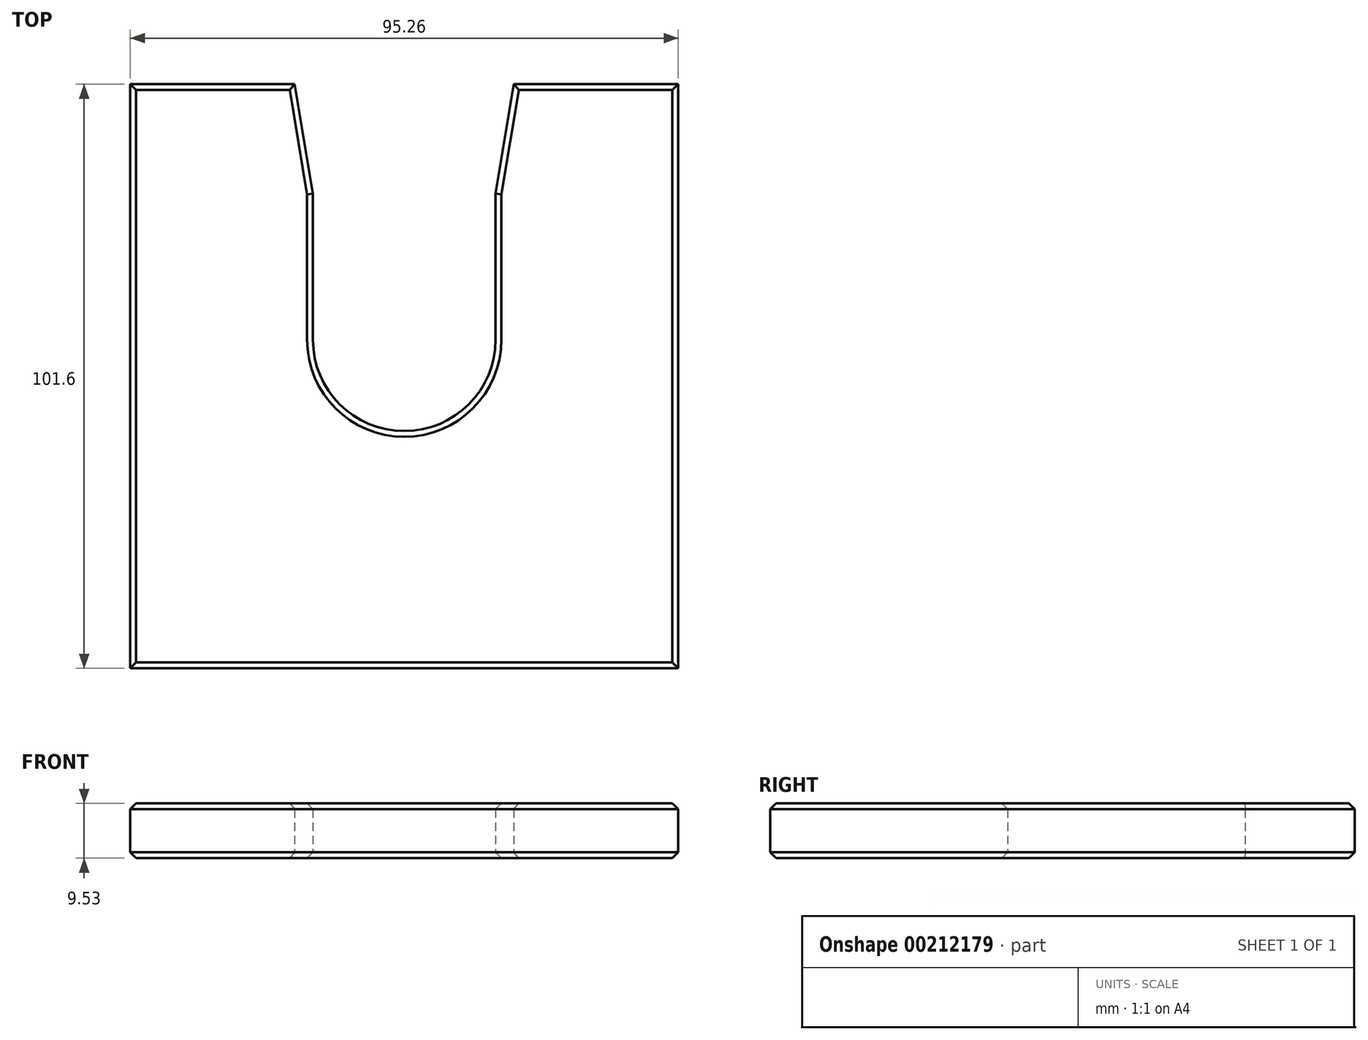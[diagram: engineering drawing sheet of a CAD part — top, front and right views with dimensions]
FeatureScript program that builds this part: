
annotation { "Feature Type Name" : "Feature", "Feature Type Description" : "" }
export const myFeature = defineFeature(function(context is Context, id is Id, definition is map)
    precondition{}
    {
        {
            var Q0;
            Q0=qCreatedBy(makeId("Top.planeOp"),FACE);
            var sketch = newSketch(context, id + "F0", { "sketchPlane" : qUnion([Q0])});
            skLineSegment(sketch, "E0.bottom", {"start": v(-47.62, 50.8) * mm, "end": v(-19.05, 50.8) * mm});
            skLineSegment(sketch, "E0.top", {"start": v(-47.63, -50.8) * mm, "end": v(47.62, -50.8) * mm});
            skLineSegment(sketch, "E0.left", {"start": v(-47.62, 50.8) * mm, "end": v(-47.63, -50.8) * mm});
            skLineSegment(sketch, "E0.right", {"start": v(47.63, 50.8) * mm, "end": v(47.62, -50.8) * mm});
            skPoint(sketch, "E0.middle", {"position": v(0, 0) * mm});
            skLineSegment(sketch, "E1", {"start": v(0, 50.8) * mm, "end": v(0, 6.35) * mm, "construction": true});
            skPoint(sketch, "E1.endSnap0", {"position": v(0, 50.8) * mm});
            skArc(sketch, "E2.0.endCap", {"start": v(15.88, 6.35) * mm, "mid": v(0, -9.53) * mm, "end": v(-15.87, 6.35) * mm});
            skLineSegment(sketch, "E2.0.left", {"start": v(15.88, 31.75) * mm, "end": v(15.88, 6.35) * mm});
            skLineSegment(sketch, "E2.0.right", {"start": v(-15.87, 31.75) * mm, "end": v(-15.87, 6.35) * mm});
            skLineSegment(sketch, "E3.0", {"start": v(-19.05, 50.8) * mm, "end": v(-19.05, 6.35) * mm, "construction": true});
            skLineSegment(sketch, "E4.0", {"start": v(19.05, 50.8) * mm, "end": v(19.05, 6.35) * mm, "construction": true});
            skLineSegment(sketch, "E5", {"start": v(19.05, 31.75) * mm, "end": v(-19.05, 31.75) * mm, "construction": true});
            skLineSegment(sketch, "E6", {"start": v(15.88, 31.75) * mm, "end": v(19.05, 50.8) * mm});
            skLineSegment(sketch, "E7", {"start": v(-15.87, 31.75) * mm, "end": v(-19.05, 50.8) * mm});
            skLineSegment(sketch, "E8.trimOffspring", {"start": v(19.05, 50.8) * mm, "end": v(47.63, 50.8) * mm});
            skLineSegment(sketch, "E9.trimOffspring", {"start": v(-15.87, 50.8) * mm, "end": v(0, 50.8) * mm});
            skSolve(sketch);
        }
        {
            var Q0;
            Q0=makeQuery(id+"F0.imprint","IMPRINT",FACE,{"disambiguationData":[TD([[makeQuery(id+"F0.imprint","IMPRINT",EDGE,{"derivedFrom":sQuery(id+"F0.wireOp",EDGE,"E0.bottom")}),-1.0]])]});
            extrude(context, id + "F1", {"entities" : qUnion([Q0]), "depth" : 9.52 * mm});
        }
        {
            var Q0;
            Q0=makeQuery(id+"F1.opExtrude","CAP_FACE",FACE,{"disambiguationData":[OSD([sQuery(id+"F0.wireOp",EDGE,"E0.bottom"),sQuery(id+"F0.wireOp",EDGE,"E0.top"),sQuery(id+"F0.wireOp",EDGE,"E0.left"),sQuery(id+"F0.wireOp",EDGE,"E0.right"),sQuery(id+"F0.wireOp",EDGE,"E2.0.endCap"),sQuery(id+"F0.wireOp",EDGE,"E2.0.left"),sQuery(id+"F0.wireOp",EDGE,"E2.0.right"),sQuery(id+"F0.wireOp",EDGE,"E6"),sQuery(id+"F0.wireOp",EDGE,"E7"),sQuery(id+"F0.wireOp",EDGE,"E8.trimOffspring")])],"isStart":false});
            var Q1;
            Q1=makeQuery(id+"F1.opExtrude","CAP_FACE",FACE,{"disambiguationData":[OSD([sQuery(id+"F0.wireOp",EDGE,"E0.bottom"),sQuery(id+"F0.wireOp",EDGE,"E0.top"),sQuery(id+"F0.wireOp",EDGE,"E0.left"),sQuery(id+"F0.wireOp",EDGE,"E0.right"),sQuery(id+"F0.wireOp",EDGE,"E2.0.endCap"),sQuery(id+"F0.wireOp",EDGE,"E2.0.left"),sQuery(id+"F0.wireOp",EDGE,"E2.0.right"),sQuery(id+"F0.wireOp",EDGE,"E6"),sQuery(id+"F0.wireOp",EDGE,"E7"),sQuery(id+"F0.wireOp",EDGE,"E8.trimOffspring")])],"isStart":true});
            chamfer(context, id + "F2", {"entities" : qUnion([Q0, Q1]), "width" : 1.02 * mm, "tangentPropagation" : true});
        }
    });
